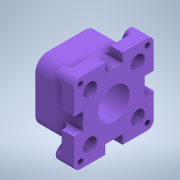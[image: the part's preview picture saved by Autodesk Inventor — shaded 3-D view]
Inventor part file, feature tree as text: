
AUTODESK INVENTOR PART (.ipt)
format: ipt  version: 2022 (Build 260153000, 153)  size: 731,648 bytes
history: native  units: mm
features: extrude x10, sketch x10, projected_geometry x8, chamfer x4, fillet x3
ambient origin geometry x8: Origin, YZ Plane, XZ Plane, XY Plane, X Axis, Y Axis, Z Axis, Center Point
bodies: Solid1 (feature_tree)
feature tree (35):
  extrude  "Extrusion1"  Depth=27.5mm
  extrude  "Extrusion4"  Depth=38.6mm
  fillet  "Fillet1"  Radius=2.5mm
  extrude  "Extrusion5"  Depth=2.5mm
  extrude  "Extrusion6"  Depth=2.5mm
  sketch  "Sketch8"  dims[d9=3.0mm d10=2.5mm]
  extrude  "Extrusion7"  Depth=2.5mm
  extrude  "Extrusion8"  Depth=7.4mm
  chamfer  "Chamfer2"  Distance=7.0mm
  chamfer  "Chamfer3"  Distance=2.0mm
  chamfer  "Chamfer4"  Distance=2.0mm
  chamfer  "Chamfer5"  Distance=2.0mm
  extrude  "Extrusion9"  Depth=1.5mm
  extrude  "Extrusion10"  Depth=1.5mm
  extrude  "Extrusion11"  Depth=1.5mm TaperAngle=0.0deg
  fillet  "Fillet2"  Radius=4.0mm
  extrude  "Extrusion12"  Depth=1.5mm
  fillet  "Fillet4"  Radius=22.0mm
  sketch  "Sketch1"  dims[d0=27.5mm d1=27.5mm]
  sketch  "Sketch5"  dims[d2=38.6mm d3=38.6mm d4=2.5mm]
  projected_geometry  "Projected Loop1"
  sketch  "Sketch6"  dims[d5=3.0mm d6=2.5mm]
  sketch  "Sketch7"  dims[d7=3.0mm d8=2.5mm]
  projected_geometry  "Projected Loop2"
  projected_geometry  "Projected Loop3"
  sketch  "Sketch9"  dims[d11=3.0mm d12=7.4mm]
  projected_geometry  "Projected Loop4"
  sketch  "Sketch11"  dims[d13=7.4mm]
  projected_geometry  "Projected Loop11"
  projected_geometry  "Projected Loop12"
  sketch  "Sketch12"  dims[d14=7.4mm]
  sketch  "Sketch13"  dims[d15=7.4mm d16=7.0mm d17=0.0mm]
  projected_geometry  "Projected Loop13"
  projected_geometry  "Projected Loop14"
  sketch  "Sketch14"  dims[d18=25.5mm d19=2.0mm d20=2.0mm d21=2.0mm d22=2.0mm d31=5.0mm d32=20.5mm d33=0.0mm d34=4.0mm d35=3.0mm d36=22.0mm d37=3.0mm d38=0.0mm d42=5.0mm d43=5.0mm d44=6.0mm d45=0.0mm d46=5.0mm d47=5.0mm d48=5.0mm d49=5.0mm d50=18.0mm d51=8.0mm d52=0.0mm d53=10.0mm d54=0.0mm d55=1.5mm d56=10.0mm d57=45.0deg d58=1.5mm d59=10.0mm d60=45.0deg d61=1.5mm d62=10.0mm d63=45.0deg d64=1.5mm d65=10.0mm d66=45.0deg d71=6.0mm d72=6.0mm d73=6.0mm d74=6.0mm d75=10.0mm d76=0.0mm d77=5.5mm d78=4.0mm d79=1.5mm d80=0.0mm d81=7.4mm d82=7.4mm d83=7.4mm d84=3.5mm d85=0.0mm d86=40.0mm d88=360.0deg d90=2.0mm d92=10.0mm d93=10.5mm d94=10.5mm d95=10.0mm d96=10.0mm d97=10.5mm d98=10.5mm d99=10.0mm d100=20.5mm d101=0.0mm d102=1.5mm]
